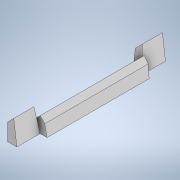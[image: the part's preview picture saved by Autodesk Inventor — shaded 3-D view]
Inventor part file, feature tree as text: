
AUTODESK INVENTOR PART (.ipt)
format: ipt  version: 2021 (Build 250183000, 183)  size: 168,448 bytes
history: native  units: in
note: dims shown in document units (in); Inventor stores cm internally (conversion verified against a paired STEP export)
features: extrude x5, sketch x5, projected_geometry x5
ambient origin geometry x8: Origin, YZ Plane, XZ Plane, XY Plane, X Axis, Y Axis, Z Axis, Center Point
bodies: Solid1 (feature_tree)
feature tree (15):
  extrude  "Extrusion1"  Depth=2.5984in TaperAngle=0.0deg
  extrude  "Extrusion2"  Depth=0.2362in
  extrude  "Extrusion8"  Depth=0.5906in TaperAngle=0.0deg
  extrude  "Extrusion11"  Depth=0.0787in
  extrude  "Extrusion12"  Depth=1.5812in TaperAngle=0.0deg
  sketch  "Sketch1"  dims[d2=45.0deg d3=2.5984in d4=0.0in]
  sketch  "Sketch2"  dims[d8=0.2362in d9=0.4331in]
  sketch  "Sketch8"  dims[d10=0.5906in d11=0.0in d25=0.5906in d26=0.0in]
  projected_geometry  "Projected Loop1"
  projected_geometry  "Projected Loop2"
  sketch  "Sketch13"  dims[d42=0.0787in d43=0.0787in]
  projected_geometry  "Projected Loop6"
  projected_geometry  "Projected Loop7"
  sketch  "Sketch15"  dims[d44=0.4813in d45=0.0in d46=1.5812in d47=0.0in d12=0.0197in d13=0.0344in d32=0.0197in d33=0.0344in d34=0.0197in d35=0.0344in]
  projected_geometry  "Projected Loop9"
